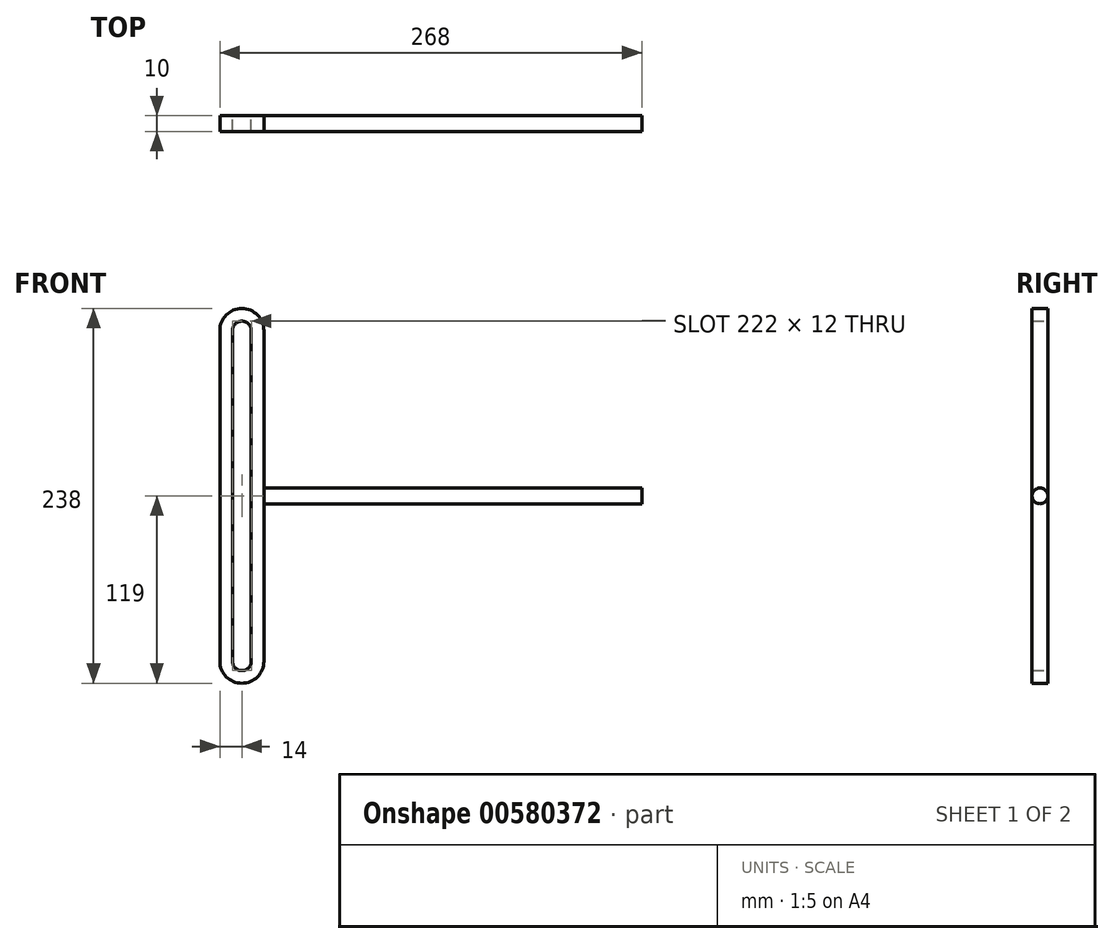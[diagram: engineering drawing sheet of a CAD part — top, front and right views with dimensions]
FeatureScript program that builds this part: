
annotation { "Feature Type Name" : "Feature", "Feature Type Description" : "" }
export const myFeature = defineFeature(function(context is Context, id is Id, definition is map)
    precondition{}
    {
        {
            var Q0;
            Q0=qCreatedBy(makeId("Front.planeOp"),FACE);
            var sketch = newSketch(context, id + "F0", { "sketchPlane" : qUnion([Q0])});
            skLineSegment(sketch, "E0.left", {"start": v(6, 105) * mm, "end": v(6, -105) * mm});
            skLineSegment(sketch, "E0.right", {"start": v(-6, 105) * mm, "end": v(-6, -105) * mm});
            skPoint(sketch, "E0.middle", {"position": v(0, 0) * mm});
            skArc(sketch, "E1", {"start": v(6, 105) * mm, "mid": v(0, 111) * mm, "end": v(-6, 105) * mm});
            skArc(sketch, "E2", {"start": v(-6, -105) * mm, "mid": v(0, -111) * mm, "end": v(6, -105) * mm});
            skLineSegment(sketch, "E3.0", {"start": v(14, 105) * mm, "end": v(14, -105) * mm});
            skArc(sketch, "E3.1", {"start": v(14, 105) * mm, "mid": v(0, 119) * mm, "end": v(-14, 105) * mm});
            skLineSegment(sketch, "E3.2", {"start": v(-14, 105) * mm, "end": v(-14, -105) * mm});
            skArc(sketch, "E3.3", {"start": v(-14, -105) * mm, "mid": v(0, -119) * mm, "end": v(14, -105) * mm});
            skSolve(sketch);
        }
        {
            var Q0;
            Q0=makeQuery(id+"F0.imprint","IMPRINT",FACE,{"disambiguationData":[TD([[makeQuery(id+"F0.imprint","IMPRINT",EDGE,{"derivedFrom":sQuery(id+"F0.wireOp",EDGE,"E0.left")}),1.0]])]});
            extrude(context, id + "F1", {"entities" : qUnion([Q0]), "endBound" : BoundingType.SYMMETRIC, "depth" : 10 * mm, "offsetDistance" : 25 * mm});
        }
        {
            var Q0;
            Q0=makeQuery(id+"F1.opExtrude","SWEPT_FACE",FACE,{"disambiguationData":[OSD([sQuery(id+"F0.wireOp",EDGE,"E3.0")])]});
            var sketch = newSketch(context, id + "F2", { "sketchPlane" : qUnion([Q0])});
            skCircle(sketch, "E4", {"center": v(0, 0) * mm, "radius": 5 * mm});
            skSolve(sketch);
        }
        {
            var Q0;
            {var subQ0=sQuery(id+"F2.wireOp",EDGE,"E4");var subQ1=sQuery(id+"F0.wireOp",EDGE,"E3.0");var subQ2=makeQuery(id+"F2.imprint","INTERSECT",VERTEX,{"derivedFrom":[makeQuery(id+"F1.opExtrude","CAP_EDGE",EDGE,{"disambiguationData":[OSD([subQ1])],"isStart":true}),subQ0]});Q0=makeQuery(id+"F2.imprint","IMPRINT",FACE,{"disambiguationData":[TD([[makeQuery(id+"F2.imprint","IMPRINT",EDGE,{"disambiguationData":[TD([[subQ2,-1.0]])],"derivedFrom":subQ0}),1.0]])]});}
            extrude(context, id + "F3", {"entities" : qUnion([Q0]), "operationType" : NewBodyOperationType.ADD, "depth" : 240 * mm, "offsetDistance" : 25 * mm});
        }
    });
